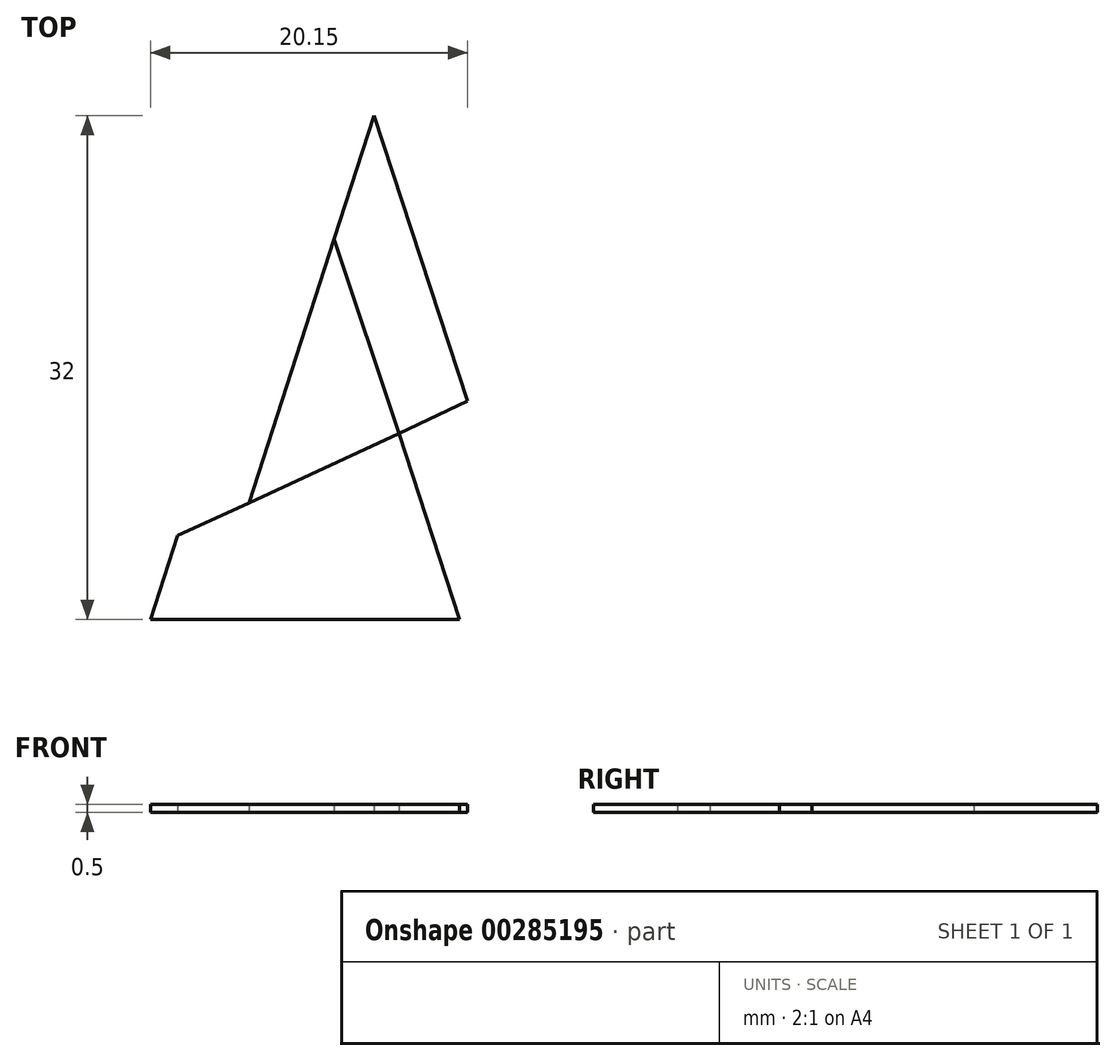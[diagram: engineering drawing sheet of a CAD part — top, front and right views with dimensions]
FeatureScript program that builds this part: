
annotation { "Feature Type Name" : "Feature", "Feature Type Description" : "" }
export const myFeature = defineFeature(function(context is Context, id is Id, definition is map)
    precondition{}
    {
        {
            var Q0;
            Q0=qCreatedBy(makeId("Top.planeOp"),FACE);
            var sketch = newSketch(context, id + "F0", { "sketchPlane" : qUnion([Q0])});
            skLineSegment(sketch, "E0", {"start": v(2.75, 18.54) * mm, "end": v(-5.17, -6.05) * mm});
            skLineSegment(sketch, "E1", {"start": v(-5.17, -6.05) * mm, "end": v(-9.7, -8.14) * mm});
            skLineSegment(sketch, "E2", {"start": v(-9.7, -8.14) * mm, "end": v(-11.44, -13.46) * mm});
            skLineSegment(sketch, "E3", {"start": v(8.18, -13.46) * mm, "end": v(4.37, -1.64) * mm});
            skLineSegment(sketch, "E4", {"start": v(4.37, -1.64) * mm, "end": v(8.7, 0.41) * mm});
            skLineSegment(sketch, "E5", {"start": v(8.7, 0.41) * mm, "end": v(2.75, 18.54) * mm});
            skLineSegment(sketch, "E6", {"start": v(-5.17, -6.05) * mm, "end": v(4.37, -1.64) * mm});
            skLineSegment(sketch, "E7", {"start": v(4.37, -1.64) * mm, "end": v(0.23, 10.7) * mm});
            skLineSegment(sketch, "E8", {"start": v(-11.44, -13.46) * mm, "end": v(8.18, -13.46) * mm});
            skSolve(sketch);
        }
        {
            var Q0;
            Q0=makeQuery(id+"F0.imprint","IMPRINT",FACE,{"disambiguationData":[TD([[makeQuery(id+"F0.imprint","IMPRINT",EDGE,{"derivedFrom":sQuery(id+"F0.wireOp",EDGE,"E4")}),1.0]])]});
            extrude(context, id + "F1", {"entities" : qUnion([Q0]), "depth" : .5 * mm});
        }
        {
            var Q0;
            {var subQ0=sQuery(id+"F0.wireOp",EDGE,"E6");Q0=makeQuery(id+"F0.imprint","IMPRINT",FACE,{"disambiguationData":[TD([[makeQuery(id+"F0.imprint","IMPRINT",EDGE,{"derivedFrom":subQ0}),1.0]])]});}
            extrude(context, id + "F2", {"entities" : qUnion([Q0]), "depth" : .5 * mm});
        }
        {
            var Q0;
            Q0=makeQuery(id+"F0.imprint","IMPRINT",FACE,{"disambiguationData":[TD([[makeQuery(id+"F0.imprint","IMPRINT",EDGE,{"derivedFrom":sQuery(id+"F0.wireOp",EDGE,"E1")}),1.0]])]});
            extrude(context, id + "F3", {"entities" : qUnion([Q0]), "depth" : .5 * mm});
        }
    });
